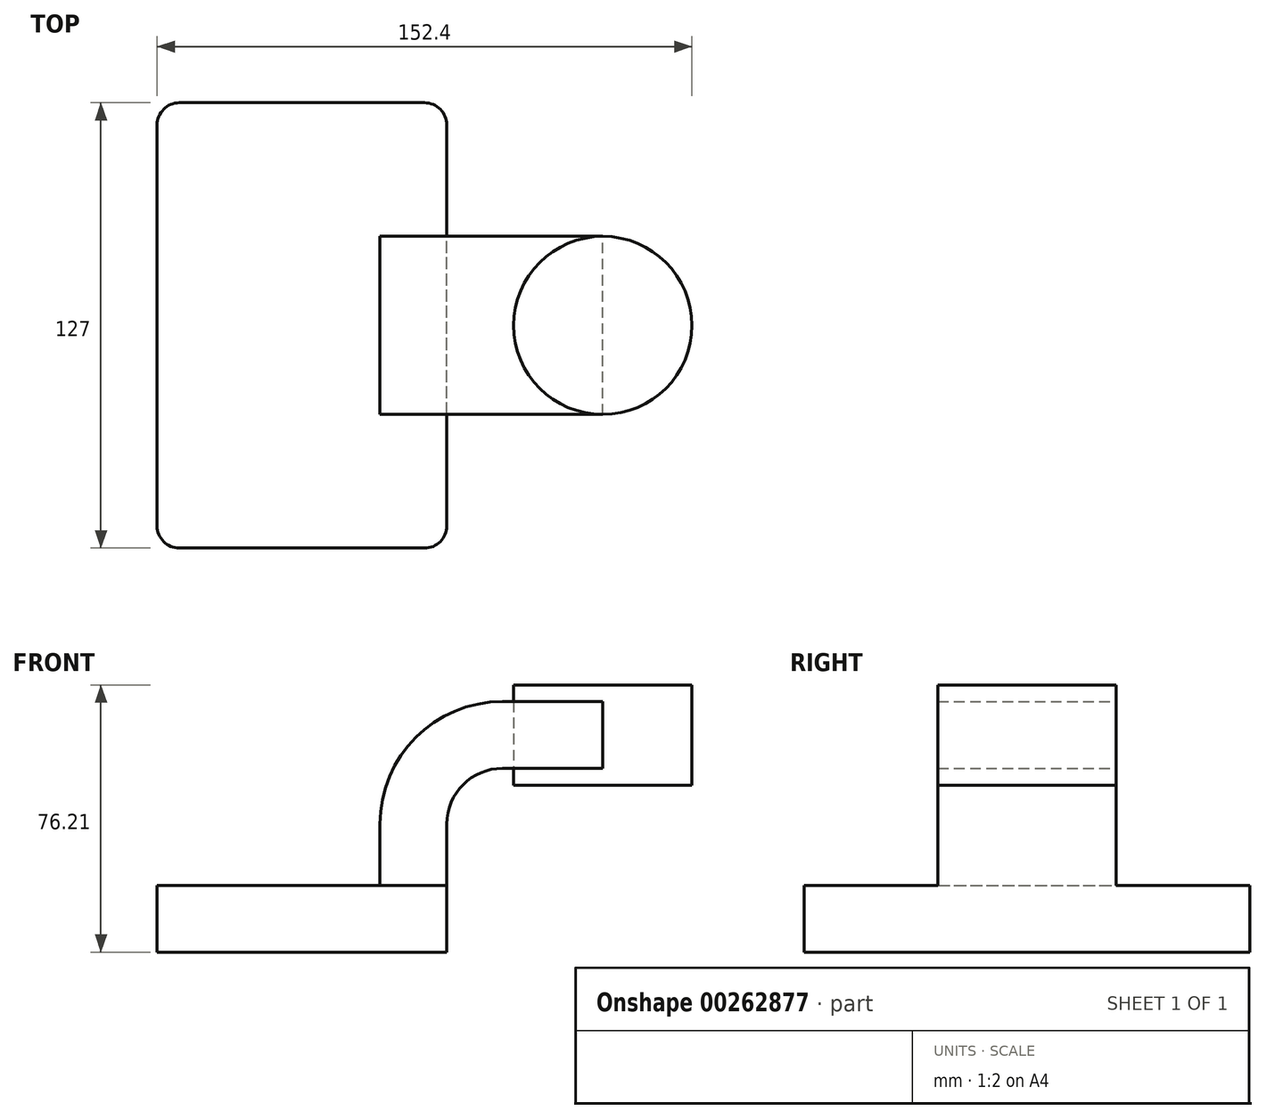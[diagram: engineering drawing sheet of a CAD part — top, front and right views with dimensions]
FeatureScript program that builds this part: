
annotation { "Feature Type Name" : "Feature", "Feature Type Description" : "" }
export const myFeature = defineFeature(function(context is Context, id is Id, definition is map)
    precondition{}
    {
        {
            var Q0;
            Q0=qCreatedBy(makeId("Front.planeOp"),FACE);
            var sketch = newSketch(context, id + "F0", { "sketchPlane" : qUnion([Q0])});
            skPoint(sketch, "E0.middle", {"position": v(0, 0) * mm});
            skLineSegment(sketch, "E1.bottom", {"start": v(-41.28, 9.53) * mm, "end": v(41.27, 9.53) * mm});
            skLineSegment(sketch, "E1.top", {"start": v(-41.28, -9.52) * mm, "end": v(41.28, -9.52) * mm});
            skLineSegment(sketch, "E1.left", {"start": v(-41.27, 9.52) * mm, "end": v(-41.27, -9.53) * mm});
            skLineSegment(sketch, "E1.right", {"start": v(41.28, 9.53) * mm, "end": v(41.28, -9.52) * mm});
            skLineSegment(sketch, "E2.bottom", {"start": v(60.32, 66.67) * mm, "end": v(111.12, 66.67) * mm});
            skLineSegment(sketch, "E2.top", {"start": v(60.32, 38.1) * mm, "end": v(111.12, 38.1) * mm});
            skLineSegment(sketch, "E2.left", {"start": v(60.32, 66.67) * mm, "end": v(60.32, 38.1) * mm});
            skLineSegment(sketch, "E2.right", {"start": v(111.13, 66.67) * mm, "end": v(111.13, 38.1) * mm});
            skPoint(sketch, "E2.middle", {"position": v(85.72, 52.39) * mm});
            skLineSegment(sketch, "E3", {"start": v(41.28, 9.53) * mm, "end": v(41.28, 27) * mm});
            skArc(sketch, "E4", {"start": v(41.27, 27) * mm, "mid": v(45.92, 38.23) * mm, "end": v(57.15, 42.88) * mm});
            skLineSegment(sketch, "E5", {"start": v(57.15, 42.88) * mm, "end": v(85.72, 42.88) * mm});
            skPoint(sketch, "E5.endSnap0", {"position": v(85.72, 38.1) * mm});
            skLineSegment(sketch, "E6.0", {"start": v(57.15, 61.93) * mm, "end": v(85.76, 61.93) * mm});
            skArc(sketch, "E6.1", {"start": v(22.23, 27) * mm, "mid": v(32.45, 51.7) * mm, "end": v(57.15, 61.93) * mm});
            skLineSegment(sketch, "E6.2", {"start": v(22.22, 9.53) * mm, "end": v(22.22, 27) * mm});
            skLineSegment(sketch, "E7", {"start": v(85.72, 38.1) * mm, "end": v(85.72, 66.67) * mm});
            skFitSpline(sketch, "E8", {"points": [v(-41.28, 9.53) * mm, v(57.15, 61.93) * mm], "startDerivative": vector(0, 76.6) * mm, "endDerivative": vector(109.35, 0) * mm});
            skSolve(sketch);
        }
        {
            var Q0;
            Q0=makeQuery(id+"F0.imprint","IMPRINT",FACE,{"disambiguationData":[TD([[makeQuery(id+"F0.imprint","IMPRINT",EDGE,{"derivedFrom":sQuery(id+"F0.wireOp",EDGE,"E1.top")}),1.0]])]});
            extrude(context, id + "F1", {"entities" : qUnion([Q0]), "endBound" : BoundingType.SYMMETRIC, "depth" : 127 * mm});
        }
        {
            var Q0;
            {var subQ1=sQuery(id+"F0.wireOp",EDGE,"E3");Q0=makeQuery(id+"F0.imprint","IMPRINT",FACE,{"disambiguationData":[TD([[makeQuery(id+"F0.imprint","IMPRINT",EDGE,{"derivedFrom":subQ1}),1.0]])]});}
            var Q1;
            {var subQ0=sQuery(id+"F0.wireOp",EDGE,"E6.0");var subQ1=sQuery(id+"F0.wireOp",EDGE,"E2.left");var subQ2=makeQuery(id+"F0.imprint","INTERSECT",VERTEX,{"derivedFrom":[subQ1,subQ0]});Q1=makeQuery(id+"F0.imprint","IMPRINT",FACE,{"disambiguationData":[TD([[makeQuery(id+"F0.imprint","IMPRINT",EDGE,{"disambiguationData":[TD([[subQ2,-1.0]])],"derivedFrom":subQ1}),1.0]])]});}
            extrude(context, id + "F2", {"entities" : qUnion([Q0, Q1]), "operationType" : NewBodyOperationType.ADD, "endBound" : BoundingType.SYMMETRIC, "depth" : 50.8 * mm});
        }
        {
            var Q0;
            Q0=makeQuery(id+"F0.imprint","IMPRINT",FACE,{"disambiguationData":[TD([[makeQuery(id+"F0.imprint","IMPRINT",EDGE,{"derivedFrom":sQuery(id+"F0.wireOp",EDGE,"E6.1")}),1.0]])]});
            extrude(context, id + "F3", {"entities" : qUnion([Q0]), "operationType" : NewBodyOperationType.ADD, "endBound" : BoundingType.SYMMETRIC, "depth" : 15.88 * mm});
        }
        {
            var Q0;
            {var subQ0=sQuery(id+"F0.wireOp",EDGE,"E2.right");Q0=makeQuery(id+"F0.imprint","IMPRINT",FACE,{"disambiguationData":[TD([[makeQuery(id+"F0.imprint","IMPRINT",EDGE,{"derivedFrom":subQ0}),-1.0]])]});}
            var Q1;
            Q1=sQuery(id+"F0.wireOp",EDGE,"E7");
            revolve(context, id + "F4", {"entities" : qUnion([Q0]), "axis" : qUnion([Q1]), "revolveType" : RevolveType.FULL});
        }
        {
            var Q0;
            Q0=makeQuery(id+"F4.opRevolve","SWEPT_BODY",BODY,{"disambiguationData":[OSD([sQuery(id+"F0.wireOp",EDGE,"E2.bottom"),sQuery(id+"F0.wireOp",EDGE,"E2.top"),sQuery(id+"F0.wireOp",EDGE,"E2.right"),sQuery(id+"F0.wireOp",EDGE,"E7")])]});
            deleteBodies(context, id + "F5", {"entities" : qUnion([Q0])});
        }
        {
            var Q0;
            {var subQ0=sQuery(id+"F0.wireOp",EDGE,"E2.right");Q0=makeQuery(id+"F0.imprint","IMPRINT",FACE,{"disambiguationData":[TD([[makeQuery(id+"F0.imprint","IMPRINT",EDGE,{"derivedFrom":subQ0}),-1.0]])]});}
            var Q1;
            Q1=sQuery(id+"F0.wireOp",EDGE,"E7");
            revolve(context, id + "F6", {"entities" : qUnion([Q0]), "axis" : qUnion([Q1]), "revolveType" : RevolveType.FULL});
        }
        {
            var Q0;
            Q0=makeQuery(id+"F1.opExtrude","CAP_EDGE",EDGE,{"disambiguationData":[OSD([sQuery(id+"F0.wireOp",EDGE,"E1.right")])],"isStart":false});
            var Q1;
            Q1=makeQuery(id+"F1.opExtrude","CAP_EDGE",EDGE,{"disambiguationData":[OSD([sQuery(id+"F0.wireOp",EDGE,"E1.left")])],"isStart":false});
            var Q2;
            Q2=makeQuery(id+"F1.opExtrude","CAP_EDGE",EDGE,{"disambiguationData":[OSD([sQuery(id+"F0.wireOp",EDGE,"E1.left")])],"isStart":true});
            var Q3;
            Q3=makeQuery(id+"F1.opExtrude","CAP_EDGE",EDGE,{"disambiguationData":[OSD([sQuery(id+"F0.wireOp",EDGE,"E1.right")])],"isStart":true});
            fillet(context, id + "F7", {"entities" : qUnion([Q0, Q1, Q2, Q3]), "radius" : 6.35 * mm, "tangentPropagation" : true, "allowEdgeOverflow" : false});
        }
    });
